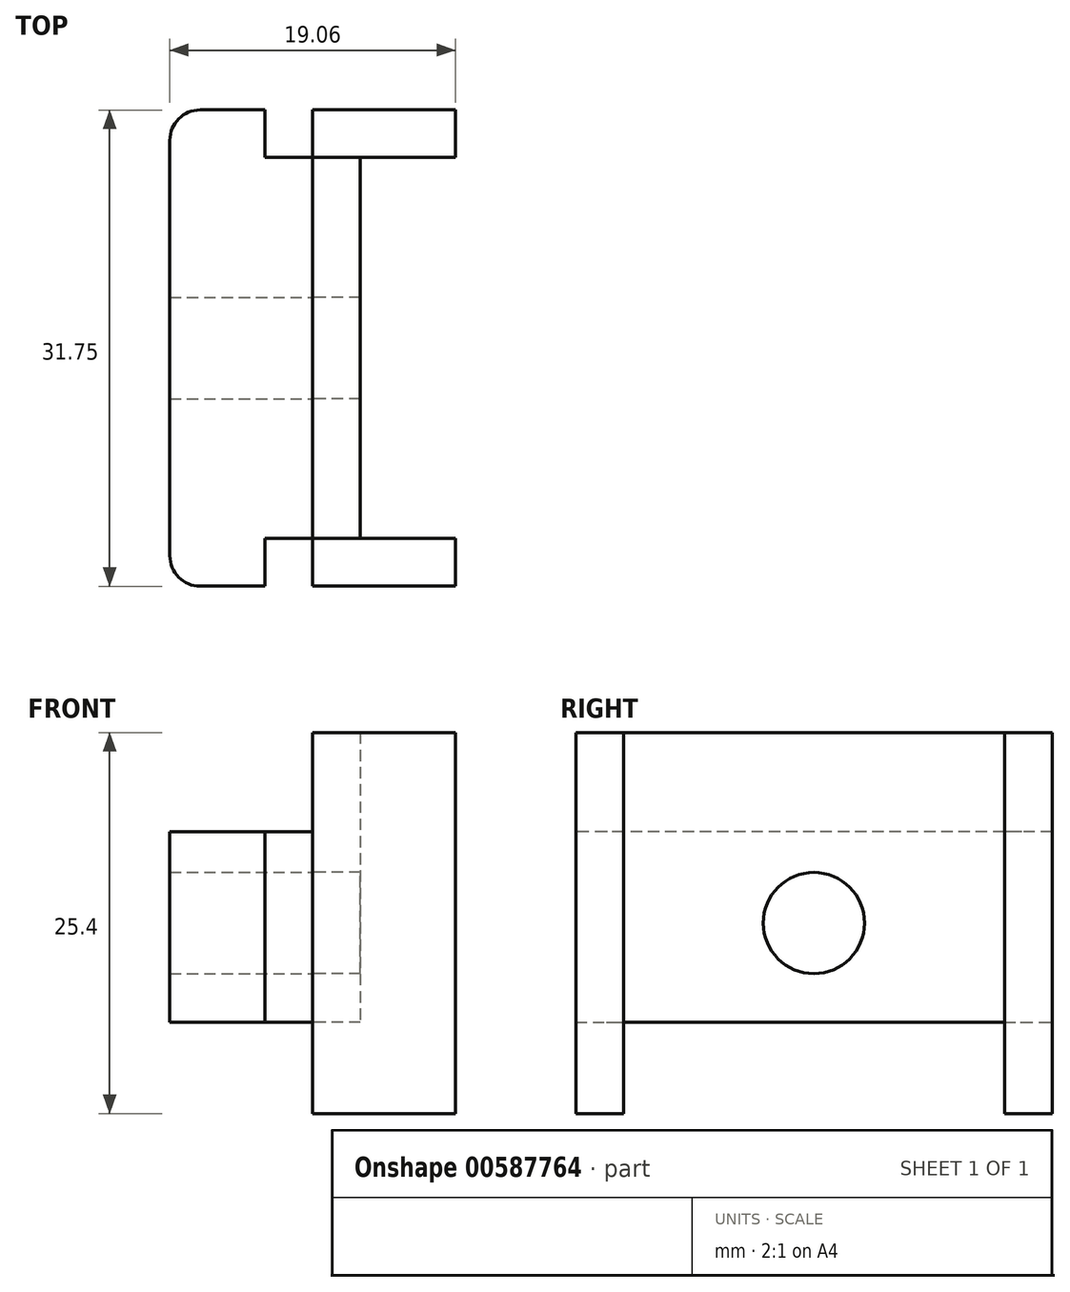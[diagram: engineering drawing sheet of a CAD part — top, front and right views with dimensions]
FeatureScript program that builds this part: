
annotation { "Feature Type Name" : "Feature", "Feature Type Description" : "" }
export const myFeature = defineFeature(function(context is Context, id is Id, definition is map)
    precondition{}
    {
        {
            var Q0;
            Q0=qCreatedBy(makeId("Right.planeOp"),FACE);
            var sketch = newSketch(context, id + "F0", { "sketchPlane" : qUnion([Q0])});
            skLineSegment(sketch, "E0", {"start": v(-6.95, -1.75) * mm, "end": v(24.8, -1.75) * mm});
            skLineSegment(sketch, "E1", {"start": v(24.8, -8.36) * mm, "end": v(-6.95, -8.36) * mm});
            skLineSegment(sketch, "E2", {"start": v(-6.95, -8.36) * mm, "end": v(-6.95, -12.17) * mm});
            skLineSegment(sketch, "E3", {"start": v(-6.95, -12.17) * mm, "end": v(-3.77, -12.17) * mm});
            skLineSegment(sketch, "E4", {"start": v(24.8, -17.25) * mm, "end": v(21.63, -17.25) * mm});
            skLineSegment(sketch, "E5", {"start": v(-6.95, -17.25) * mm, "end": v(-6.95, -21.06) * mm});
            skLineSegment(sketch, "E6", {"start": v(-6.95, -21.06) * mm, "end": v(24.8, -21.06) * mm});
            skLineSegment(sketch, "E7", {"start": v(24.8, -27.15) * mm, "end": v(-6.95, -27.15) * mm});
            skLineSegment(sketch, "E8", {"start": v(-6.95, -27.15) * mm, "end": v(-6.95, -1.75) * mm});
            skLineSegment(sketch, "E9", {"start": v(-3.77, -1.75) * mm, "end": v(-3.77, -27.15) * mm});
            skLineSegment(sketch, "E10", {"start": v(-3.77, -27.15) * mm, "end": v(21.63, -27.15) * mm});
            skLineSegment(sketch, "E11", {"start": v(21.63, -27.15) * mm, "end": v(21.63, -1.75) * mm});
            skLineSegment(sketch, "E12", {"start": v(24.8, -1.75) * mm, "end": v(24.8, -27.15) * mm});
            skPoint(sketch, "E13.endSnap0", {"position": v(24.8, -14.45) * mm});
            skPoint(sketch, "E13.endSnap1", {"position": v(8.93, -17.25) * mm});
            skCircle(sketch, "E14", {"center": v(8.93, -14.45) * mm, "radius": 3.37 * mm});
            skLineSegment(sketch, "E15.trimOffspring", {"start": v(-3.77, -17.25) * mm, "end": v(-6.95, -17.25) * mm});
            skLineSegment(sketch, "E16.trimOffspring", {"start": v(21.63, -12.17) * mm, "end": v(24.8, -12.17) * mm});
            skSolve(sketch);
        }
        {
            var Q0;
            {var subQ0=sQuery(id+"F0.wireOp",EDGE,"E12");var subQ1=sQuery(id+"F0.wireOp",EDGE,"E0");var subQ2=makeQuery(id+"F0.imprint","INTERSECT",VERTEX,{"derivedFrom":[subQ1,subQ0]});Q0=makeQuery(id+"F0.imprint","IMPRINT",FACE,{"disambiguationData":[TD([[makeQuery(id+"F0.imprint","IMPRINT",EDGE,{"disambiguationData":[TD([[subQ2,1.0]])],"derivedFrom":subQ1}),-1.0]])]});}
            var Q1;
            {var subQ0=sQuery(id+"F0.wireOp",EDGE,"E12");var subQ1=sQuery(id+"F0.wireOp",EDGE,"E1");var subQ2=makeQuery(id+"F0.imprint","INTERSECT",VERTEX,{"derivedFrom":[subQ1,subQ0]});Q1=makeQuery(id+"F0.imprint","IMPRINT",FACE,{"disambiguationData":[TD([[makeQuery(id+"F0.imprint","IMPRINT",EDGE,{"disambiguationData":[TD([[subQ2,-1.0]])],"derivedFrom":subQ1}),1.0]])]});}
            var Q2;
            {var subQ0=sQuery(id+"F0.wireOp",EDGE,"E12");var subQ1=sQuery(id+"F0.wireOp",EDGE,"E3");var subQ2=makeQuery(id+"F0.imprint","INTERSECT",VERTEX,{"derivedFrom":[subQ1,subQ0]});Q2=makeQuery(id+"F0.imprint","IMPRINT",FACE,{"disambiguationData":[TD([[makeQuery(id+"F0.imprint","IMPRINT",EDGE,{"disambiguationData":[TD([[subQ2,1.0]])],"derivedFrom":subQ1}),-1.0]])]});}
            var Q3;
            {var subQ0=sQuery(id+"F0.wireOp",EDGE,"E12");var subQ1=sQuery(id+"F0.wireOp",EDGE,"E4");var subQ2=makeQuery(id+"F0.imprint","INTERSECT",VERTEX,{"derivedFrom":[subQ1,subQ0]});Q3=makeQuery(id+"F0.imprint","IMPRINT",FACE,{"disambiguationData":[TD([[makeQuery(id+"F0.imprint","IMPRINT",EDGE,{"disambiguationData":[TD([[subQ2,-1.0]])],"derivedFrom":subQ1}),1.0]])]});}
            var Q4;
            {var subQ0=sQuery(id+"F0.wireOp",EDGE,"E12");var subQ1=sQuery(id+"F0.wireOp",EDGE,"E6");var subQ2=makeQuery(id+"F0.imprint","INTERSECT",VERTEX,{"derivedFrom":[subQ1,subQ0]});Q4=makeQuery(id+"F0.imprint","IMPRINT",FACE,{"disambiguationData":[TD([[makeQuery(id+"F0.imprint","IMPRINT",EDGE,{"disambiguationData":[TD([[subQ2,1.0]])],"derivedFrom":subQ1}),-1.0]])]});}
            var Q5;
            {var subQ0=sQuery(id+"F0.wireOp",EDGE,"E8");var subQ1=sQuery(id+"F0.wireOp",EDGE,"E6");var subQ2=makeQuery(id+"F0.imprint","INTERSECT",VERTEX,{"derivedFrom":[subQ1,subQ0]});Q5=makeQuery(id+"F0.imprint","IMPRINT",FACE,{"disambiguationData":[TD([[makeQuery(id+"F0.imprint","IMPRINT",EDGE,{"disambiguationData":[TD([[subQ2,-1.0]])],"derivedFrom":subQ1}),-1.0]])]});}
            var Q6;
            {var subQ0=sQuery(id+"F0.wireOp",EDGE,"E8");var subQ1=sQuery(id+"F0.wireOp",EDGE,"E4");var subQ2=makeQuery(id+"F0.imprint","INTERSECT",VERTEX,{"derivedFrom":[subQ1,subQ0]});Q6=makeQuery(id+"F0.imprint","IMPRINT",FACE,{"disambiguationData":[TD([[makeQuery(id+"F0.imprint","IMPRINT",EDGE,{"disambiguationData":[TD([[subQ2,1.0]])],"derivedFrom":subQ1}),1.0]])]});}
            var Q7;
            {var subQ0=sQuery(id+"F0.wireOp",EDGE,"E8");var subQ1=sQuery(id+"F0.wireOp",EDGE,"E3");var subQ2=makeQuery(id+"F0.imprint","INTERSECT",VERTEX,{"derivedFrom":[subQ1,subQ0]});Q7=makeQuery(id+"F0.imprint","IMPRINT",FACE,{"disambiguationData":[TD([[makeQuery(id+"F0.imprint","IMPRINT",EDGE,{"disambiguationData":[TD([[subQ2,-1.0]])],"derivedFrom":subQ1}),-1.0]])]});}
            var Q8;
            {var subQ0=sQuery(id+"F0.wireOp",EDGE,"E8");var subQ1=sQuery(id+"F0.wireOp",EDGE,"E1");var subQ2=makeQuery(id+"F0.imprint","INTERSECT",VERTEX,{"derivedFrom":[subQ1,subQ0]});Q8=makeQuery(id+"F0.imprint","IMPRINT",FACE,{"disambiguationData":[TD([[makeQuery(id+"F0.imprint","IMPRINT",EDGE,{"disambiguationData":[TD([[subQ2,1.0]])],"derivedFrom":subQ1}),1.0]])]});}
            var Q9;
            {var subQ0=sQuery(id+"F0.wireOp",EDGE,"E8");var subQ1=sQuery(id+"F0.wireOp",EDGE,"E0");var subQ2=makeQuery(id+"F0.imprint","INTERSECT",VERTEX,{"derivedFrom":[subQ1,subQ0]});Q9=makeQuery(id+"F0.imprint","IMPRINT",FACE,{"disambiguationData":[TD([[makeQuery(id+"F0.imprint","IMPRINT",EDGE,{"disambiguationData":[TD([[subQ2,-1.0]])],"derivedFrom":subQ1}),-1.0]])]});}
            var Q10;
            {var subQ5=sQuery(id+"F0.wireOp",EDGE,"E15.trimOffspring");Q10=makeQuery(id+"F0.imprint","IMPRINT",FACE,{"disambiguationData":[TD([[makeQuery(id+"F0.imprint","IMPRINT",EDGE,{"derivedFrom":subQ5}),1.0]])]});}
            var Q11;
            {var subQ0=sQuery(id+"F0.wireOp",EDGE,"E4");Q11=makeQuery(id+"F0.imprint","IMPRINT",FACE,{"disambiguationData":[TD([[makeQuery(id+"F0.imprint","IMPRINT",EDGE,{"derivedFrom":subQ0}),-1.0]])]});}
            extrude(context, id + "F1", {"entities" : qUnion([Q0, Q1, Q2, Q3, Q4, Q5, Q6, Q7, Q8, Q9, Q10, Q11]), "depth" : 9.52 * mm, "offsetDistance" : 25.4 * mm});
        }
        {
            var Q0;
            Q0=makeQuery(id+"F0.imprint","IMPRINT",FACE,{"disambiguationData":[TD([[makeQuery(id+"F0.imprint","IMPRINT",EDGE,{"derivedFrom":sQuery(id+"F0.wireOp",EDGE,"E14")}),-1.0]])]});
            extrude(context, id + "F2", {"entities" : qUnion([Q0]), "depth" : -9.52 * mm, "offsetDistance" : 25.4 * mm});
        }
        {
            var Q0;
            {var subQ0=sQuery(id+"F0.wireOp",EDGE,"E9");var subQ1=sQuery(id+"F0.wireOp",EDGE,"E0");var subQ2=makeQuery(id+"F0.imprint","INTERSECT",VERTEX,{"derivedFrom":[subQ1,subQ0]});Q0=makeQuery(id+"F0.imprint","IMPRINT",FACE,{"disambiguationData":[TD([[makeQuery(id+"F0.imprint","IMPRINT",EDGE,{"disambiguationData":[TD([[subQ2,-1.0]])],"derivedFrom":subQ1}),-1.0]])]});}
            var Q1;
            {var subQ0=sQuery(id+"F0.wireOp",EDGE,"E11");var subQ1=sQuery(id+"F0.wireOp",EDGE,"E1");var subQ2=makeQuery(id+"F0.imprint","INTERSECT",VERTEX,{"derivedFrom":[subQ1,subQ0]});Q1=makeQuery(id+"F0.imprint","IMPRINT",FACE,{"disambiguationData":[TD([[makeQuery(id+"F0.imprint","IMPRINT",EDGE,{"disambiguationData":[TD([[subQ2,-1.0]])],"derivedFrom":subQ1}),1.0]])]});}
            var Q2;
            {var subQ5=sQuery(id+"F0.wireOp",EDGE,"E10");Q2=makeQuery(id+"F0.imprint","IMPRINT",FACE,{"disambiguationData":[TD([[makeQuery(id+"F0.imprint","IMPRINT",EDGE,{"derivedFrom":subQ5}),1.0]])]});}
            extrude(context, id + "F3", {"entities" : qUnion([Q0, Q1, Q2]), "depth" : 3.17 * mm, "offsetDistance" : 25.4 * mm});
        }
        {
            var Q0;
            {var subQ0=sQuery(id+"F0.wireOp",EDGE,"E3");Q0=makeQuery(id+"F0.imprint","IMPRINT",FACE,{"disambiguationData":[TD([[makeQuery(id+"F0.imprint","IMPRINT",EDGE,{"derivedFrom":subQ0}),-1.0]])]});}
            var Q1;
            {var subQ0=sQuery(id+"F0.wireOp",EDGE,"E4");Q1=makeQuery(id+"F0.imprint","IMPRINT",FACE,{"disambiguationData":[TD([[makeQuery(id+"F0.imprint","IMPRINT",EDGE,{"derivedFrom":subQ0}),-1.0]])]});}
            var Q2;
            {var subQ0=sQuery(id+"F0.wireOp",EDGE,"E4");Q2=makeQuery(id+"F0.imprint","IMPRINT",FACE,{"disambiguationData":[TD([[makeQuery(id+"F0.imprint","IMPRINT",EDGE,{"derivedFrom":subQ0}),1.0]])]});}
            var Q3;
            {var subQ5=sQuery(id+"F0.wireOp",EDGE,"E16.trimOffspring");Q3=makeQuery(id+"F0.imprint","IMPRINT",FACE,{"disambiguationData":[TD([[makeQuery(id+"F0.imprint","IMPRINT",EDGE,{"derivedFrom":subQ5}),1.0]])]});}
            var Q4;
            {var subQ5=sQuery(id+"F0.wireOp",EDGE,"E15.trimOffspring");Q4=makeQuery(id+"F0.imprint","IMPRINT",FACE,{"disambiguationData":[TD([[makeQuery(id+"F0.imprint","IMPRINT",EDGE,{"derivedFrom":subQ5}),1.0]])]});}
            var Q5;
            {var subQ5=sQuery(id+"F0.wireOp",EDGE,"E3");Q5=makeQuery(id+"F0.imprint","IMPRINT",FACE,{"disambiguationData":[TD([[makeQuery(id+"F0.imprint","IMPRINT",EDGE,{"derivedFrom":subQ5}),1.0]])]});}
            extrude(context, id + "F4", {"entities" : qUnion([Q0, Q1, Q2, Q3, Q4, Q5]), "operationType" : NewBodyOperationType.ADD, "depth" : -9.52 * mm, "offsetDistance" : 25.4 * mm, "hasSecondDirection" : true, "secondDirectionOppositeDirection" : true, "secondDirectionDepth" : 3.17 * mm});
        }
        {
            var Q0;
            Q0=makeQuery(id+"F4.opExtrude","CAP_EDGE",EDGE,{"disambiguationData":[OSD([sQuery(id+"F0.wireOp",EDGE,"E8")])],"isStart":false});
            var Q1;
            Q1=makeQuery(id+"F4.opExtrude","CAP_EDGE",EDGE,{"disambiguationData":[OSD([sQuery(id+"F0.wireOp",EDGE,"E12")])],"isStart":false});
            fillet(context, id + "F5", {"entities" : qUnion([Q0, Q1]), "radius" : 2.03 * mm, "tangentPropagation" : true, "allowEdgeOverflow" : false});
        }
    });
